# Revit family: Bottle _Filling_Station-Elkay-EZS8WS_LK_SK
name_source: partatom
category: Plumbing Fixtures
units: mm (PartAtom-declared; Revit-internal decimal feet)

## family parameters
Always vertical = Yes
Cut with Voids When Loaded = No
Maintain Annotation Orientation = No
OmniClass Number = 23.65.70.14.11
OmniClass Title = Drinking Fountains/Coolers
Part Type = Normal
Room Calculation Point = No
Round Connector Dimension = Use Diameter
Shared = No
Work Plane-Based = No

## types (2) — shared parameters
Activation Method = Electronic Bottle Filler Sensor with Electronic Front and Side Bubbler Pushbar
Approx. Shipping Weight (lbs) = 82
Assembly Code = D2010800
Chilling Capacity (GPH) = 8
Connector Outlet B = 1.25 "
Connector Supply A = 0.375 "
Current = 0 A
Inlet Connection Size (inch) = 0.375 "
Main Material = Finish-Elkay-Steel
Manufacturer = Elkay Manufacturer Company
Manufacturer Brand = Elkay (by Zurn Elkay Water Solutions)
Masking Arc Radius = 21 "
Material_Bubbler = Finish-Elkay-Yellow
Number of Poles = 1
Outlet Connection Size (inch) = 1.25 "
Power Factor = 1
Product Documentation Link = https://www.elkayfiles.com
Product Installation Sheet URL = https://www.elkayfiles.com
Product Page URL = https://www.elkay.com
Product data URL = https://bimobject.com
Repair Parts URL = https://www.elkayfiles.com
URL = https://www.elkay.com
Voltage = 115 V
zero-valued in all types: CWFU, Default Elevation, HWFU, WFU

## per-type parameters (varying)
| type | Description | Material_Basin | Material_Bottle Filler | Material_Wrapper | Model | Product Weight (lbs) |
| EZS8WSSK (Bottle Filling Station with Single ADA Cooler) | Elkay ezH2O® Bottle Filling Station with Single ADA Cooler Non-Filtered Refrigerated Stainless | Finish-Elkay-Plastic-1 | Finish-Elkay-Plastic-1 | Finish-Elkay-Steel | EZS8WSSK | 71 |
| EZS8WSLK ( Bottle Filling Station with Single ADA Cooler) | ezH2O® Bottle Filling Station with Single ADA Cooler Non-Filtered Refrigerated Light Gray | Finish-Elkay-Plastic | Finish-Elkay-Plastic | Finish-Elkay-Light Gray(1) | EZS8WSLK | 69 |

## geometry (parser evidence)
native form markers: Sweep x13
no freeform markers — native parametric forms only
